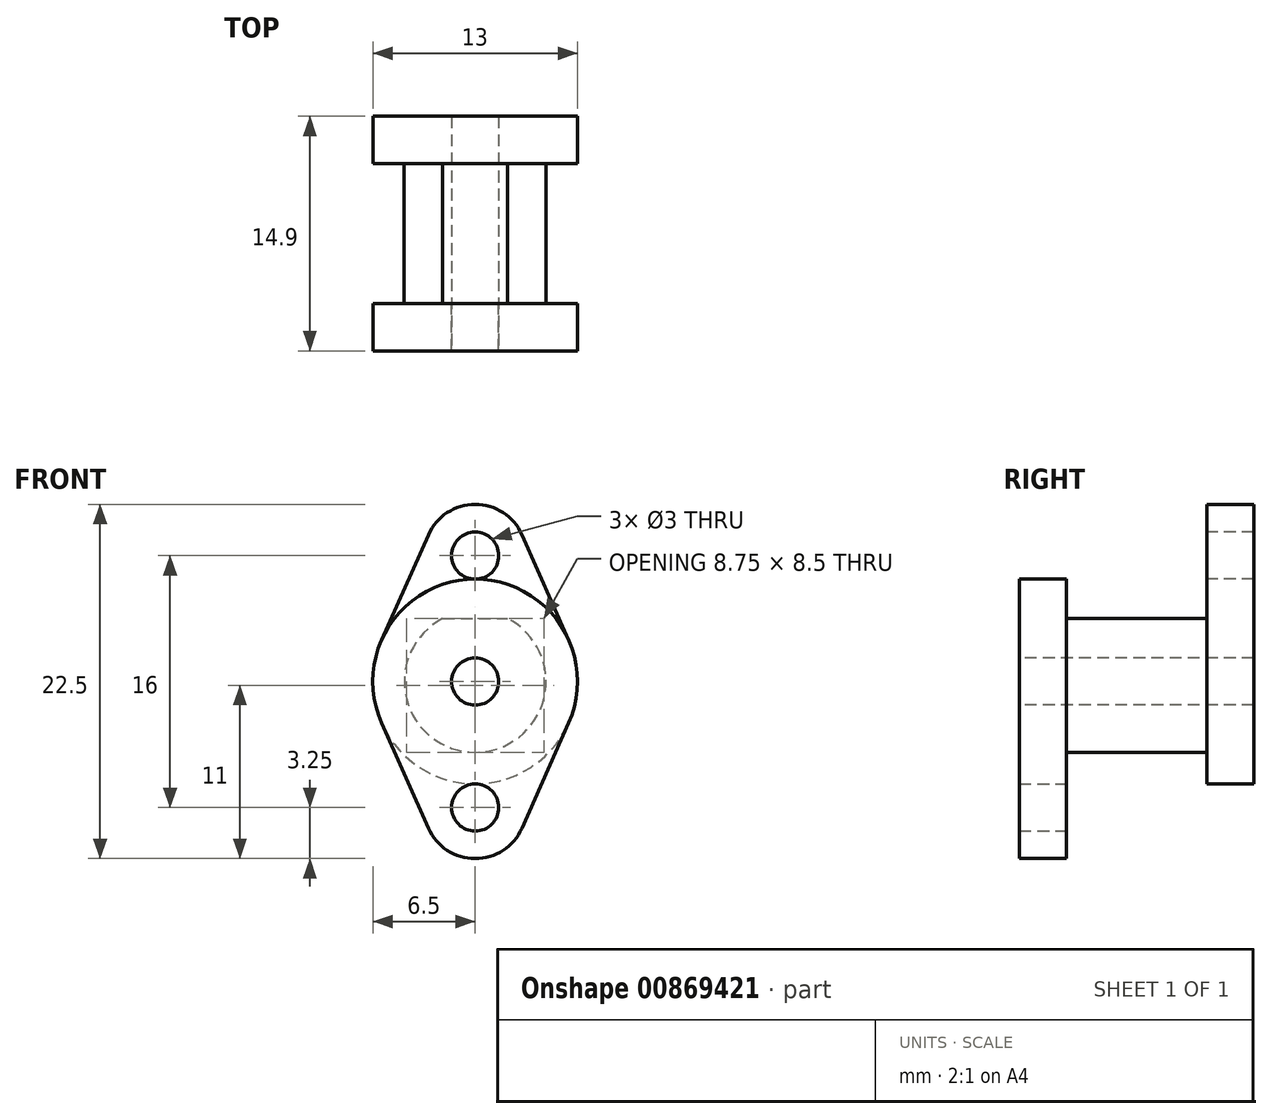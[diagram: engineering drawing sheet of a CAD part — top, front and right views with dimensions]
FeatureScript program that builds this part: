
annotation { "Feature Type Name" : "Feature", "Feature Type Description" : "" }
export const myFeature = defineFeature(function(context is Context, id is Id, definition is map)
    precondition{}
    {
        {
            var Q0;
            Q0=qCreatedBy(makeId("Front.planeOp"),FACE);
            var sketch = newSketch(context, id + "F0", { "sketchPlane" : qUnion([Q0])});
            skArc(sketch, "E0", {"start": v(2.97, 9.32) * mm, "mid": v(0, 11.25) * mm, "end": v(-2.97, 9.32) * mm});
            skCircle(sketch, "E1", {"center": v(0, 0) * mm, "radius": 1.5 * mm, "construction": true});
            skArc(sketch, "E2", {"start": v(-5.94, 2.64) * mm, "mid": v(0, -6.5) * mm, "end": v(5.94, 2.64) * mm});
            skLineSegment(sketch, "E3", {"start": v(-2.97, 9.32) * mm, "end": v(-5.94, 2.64) * mm});
            skLineSegment(sketch, "E4", {"start": v(2.97, 9.32) * mm, "end": v(5.94, 2.64) * mm});
            skCircle(sketch, "E5", {"center": v(0, 8) * mm, "radius": 1.5 * mm});
            skSolve(sketch);
        }
        {
            var Q0;
            Q0=makeQuery(id+"F0.imprint","IMPRINT",FACE,{"disambiguationData":[TD([[makeQuery(id+"F0.imprint","IMPRINT",EDGE,{"derivedFrom":sQuery(id+"F0.wireOp",EDGE,"E0")}),1.0]])]});
            extrude(context, id + "F1", {"entities" : qUnion([Q0]), "oppositeDirection" : true, "depth" : 3 * mm, "offsetDistance" : 25 * mm});
        }
        {
            var Q0;
            Q0=makeQuery(id+"F1.opExtrude","CAP_FACE",FACE,{"disambiguationData":[OSD([sQuery(id+"F0.wireOp",EDGE,"E0"),sQuery(id+"F0.wireOp",EDGE,"E2"),sQuery(id+"F0.wireOp",EDGE,"E3"),sQuery(id+"F0.wireOp",EDGE,"E4"),sQuery(id+"F0.wireOp",EDGE,"E5")])],"isStart":true});
            var sketch = newSketch(context, id + "F2", { "sketchPlane" : qUnion([Q0])});
            skCircle(sketch, "E6", {"center": v(0, 0) * mm, "radius": 4.5 * mm});
            skLineSegment(sketch, "E7", {"start": v(-2.06, 4) * mm, "end": v(2.06, 4) * mm});
            skSolve(sketch);
        }
        {
            var Q0;
            {var subQ0=sQuery(id+"F2.wireOp",EDGE,"E7");Q0=makeQuery(id+"F2.imprint","IMPRINT",FACE,{"disambiguationData":[TD([[makeQuery(id+"F2.imprint","IMPRINT",EDGE,{"derivedFrom":subQ0}),-1.0]])]});}
            extrude(context, id + "F3", {"entities" : qUnion([Q0]), "operationType" : NewBodyOperationType.ADD, "depth" : 8.9 * mm, "offsetDistance" : 25 * mm});
        }
        {
            var Q0;
            Q0=makeQuery(id+"F3.opExtrude","CAP_FACE",FACE,{"disambiguationData":[OSD([sQuery(id+"F2.wireOp",EDGE,"E6")])],"isStart":false});
            var sketch = newSketch(context, id + "F4", { "sketchPlane" : qUnion([Q0])});
            skCircle(sketch, "E8", {"center": v(0, 0) * mm, "radius": 1.5 * mm});
            skSolve(sketch);
        }
        {
            var Q0;
            Q0=makeQuery(id+"F4.imprint","IMPRINT",FACE,{"disambiguationData":[TD([[makeQuery(id+"F4.imprint","IMPRINT",EDGE,{"derivedFrom":sQuery(id+"F4.wireOp",EDGE,"E8")}),1.0]])]});
            extrude(context, id + "F5", {"entities" : qUnion([Q0]), "operationType" : NewBodyOperationType.REMOVE, "oppositeDirection" : true, "depth" : 20 * mm, "offsetDistance" : 25 * mm});
        }
        {
            var Q0;
            Q0=makeQuery(id+"F3.opExtrude","CAP_FACE",FACE,{"disambiguationData":[OSD([sQuery(id+"F2.wireOp",EDGE,"E6"),sQuery(id+"F2.wireOp",EDGE,"E7")])],"isStart":false});
            var sketch = newSketch(context, id + "F6", { "sketchPlane" : qUnion([Q0])});
            skCircle(sketch, "E9.0", {"center": v(0, 8) * mm, "radius": 1.5 * mm, "construction": true});
            skArc(sketch, "E10.0", {"start": v(2.97, 9.32) * mm, "mid": v(0, 11.25) * mm, "end": v(-2.97, 9.32) * mm, "construction": true});
            skLineSegment(sketch, "E11.0", {"start": v(-2.97, 9.32) * mm, "end": v(-5.94, 2.64) * mm, "construction": true});
            skArc(sketch, "E12.0", {"start": v(-5.94, 2.64) * mm, "mid": v(0, -6.5) * mm, "end": v(5.94, 2.64) * mm, "construction": true});
            skCircle(sketch, "E13.0", {"center": v(0, 0) * mm, "radius": 1.5 * mm, "construction": true});
            skLineSegment(sketch, "E14.0", {"start": v(2.97, 9.32) * mm, "end": v(5.94, 2.64) * mm, "construction": true});
            skLineSegment(sketch, "E15.MirrorCS", {"start": v(-2.97, -9.32) * mm, "end": v(-5.94, -2.64) * mm});
            skArc(sketch, "E16.MirrorCS", {"start": v(2.97, -9.32) * mm, "mid": v(0, -11.25) * mm, "end": v(-2.97, -9.32) * mm});
            skLineSegment(sketch, "E17.MirrorCS", {"start": v(2.97, -9.32) * mm, "end": v(5.94, -2.64) * mm});
            skArc(sketch, "E18.MirrorCS", {"start": v(-5.94, -2.64) * mm, "mid": v(0, 6.5) * mm, "end": v(5.94, -2.64) * mm});
            skCircle(sketch, "E19.MirrorC", {"center": v(0, -8) * mm, "radius": 1.5 * mm});
            skArc(sketch, "E20.MirrorCS", {"start": v(-5.94, -2.64) * mm, "mid": v(0, 6.5) * mm, "end": v(5.94, -2.64) * mm, "construction": true});
            skSolve(sketch);
        }
        {
            var Q0;
            Q0=makeQuery(id+"F6.imprint","IMPRINT",FACE,{"disambiguationData":[TD([[makeQuery(id+"F6.imprint","IMPRINT",EDGE,{"derivedFrom":sQuery(id+"F6.wireOp",EDGE,"E15.MirrorCS")}),-1.0]])]});
            var Q1;
            Q1=makeQuery(id+"F6.imprint","IMPRINT",FACE,{"disambiguationData":[TD([[makeQuery(id+"F6.imprint","IMPRINT",EDGE,{"derivedFrom":makeQuery(id+"F3.opExtrude","CAP_EDGE",EDGE,{"disambiguationData":[OSD([sQuery(id+"F2.wireOp",EDGE,"E6")])],"isStart":false})}),1.0]])]});
            extrude(context, id + "F7", {"entities" : qUnion([Q0, Q1]), "operationType" : NewBodyOperationType.ADD, "depth" : 3 * mm, "offsetDistance" : 25 * mm});
        }
    });
